# Revit family: 876-01-001-DN400-1200
name_source: partatom
category: Pipe Accessories
units: mm (PartAtom-declared; Revit-internal decimal feet)

## family parameters
Always vertical = Yes
Cut with Voids When Loaded = No
Part Type = Valve - Breaks Into
Round Connector Dimension = Use Diameter
Shared = No
Work Plane-Based = No

## types (18) — shared parameters
3 = 3 mm  [stored 0.00984252 ft]
876-0400-01-01102012 = DN400_PN10
876-0400-01-11102012 = DN400_PN16
876-0450-01-01102012 = DN450_PN10
876-0450-01-11102012 = DN450_PN16
876-0500-01-01102012 = DN500_PN10
876-0500-01-11102012 = DN500_PN16
876-0600-01-01102012 = DN600_PN10
876-0600-01-11102012 = DN600_PN16
876-0700-01-01102012 = DN700_PN10
876-0700-01-11102012 = DN700_PN16
876-0800-01-01102012 = DN800_PN10
876-0800-01-11102012 = DN800_PN16
876-0900-01-01102012 = DN900_PN10
876-0900-01-11102012 = DN900_PN16
876-1000-01-01102012 = DN1000_PN10
876-1000-01-11102012 = DN1000_PN16
876-1200-01-01102012 = DN1200_PN10
876-1200-01-11102012 = DN1200_PN16
Description_ = AVK NOZZLE CHECK VALVE, MULTI STEM
Search_table = 876-01-001-DN400-1200
URL product pages = https://www.avkvalves.com

## per-type parameters (varying)
| type | Bodywall_thickness | D | D1 | D2 | DN | Flange_thickness | Flange_thickness_2 | Flange_thickness_3 | Flange_thickness_4 | ID | ID_ref | ID_ref_2 | L | L1 | PCD |
| DN0400_PN10 | 210 mm  [stored 0.688976 ft] | 283 mm | 515 mm | 240 mm  [stored 0.787402 ft] | 400 mm | 20 mm  [stored 0.0656168 ft] | 10 mm  [stored 0.0328084 ft] | 30 mm  [stored 0.0984252 ft] | 40 mm  [stored 0.131234 ft] | 200 mm  [stored 0.656168 ft] | 180 mm  [stored 0.590551 ft] | 90 mm  [stored 0.295276 ft] | 310 mm | 1 mm  [stored 0.00328084 ft] | 127 mm |
| DN0400_PN16 | 210 mm  [stored 0.688976 ft] | 290 mm | 525 mm | 240 mm  [stored 0.787402 ft] | 400 mm | 20 mm  [stored 0.0656168 ft] | 10 mm  [stored 0.0328084 ft] | 30 mm  [stored 0.0984252 ft] | 40 mm  [stored 0.131234 ft] | 200 mm  [stored 0.656168 ft] | 180 mm  [stored 0.590551 ft] | 90 mm  [stored 0.295276 ft] | 310 mm | 1 mm  [stored 0.00328084 ft] | 127 mm |
| DN0450_PN16 | 235 mm  [stored 0.770997 ft] | 320 mm | 585 mm | 274 mm | 450 mm | 30 mm  [stored 0.0984252 ft] | 15 mm  [stored 0.0492126 ft] | 45 mm  [stored 0.147638 ft] | 60 mm  [stored 0.19685 ft] | 225 mm  [stored 0.738189 ft] | 195 mm  [stored 0.639764 ft] | 98 mm | 330 mm | 7 mm  [stored 0.0229659 ft] | 140 mm  [stored 0.459318 ft] |
| DN0500_PN10 | 260 mm | 335 mm | 620 mm | 291 mm | 500 mm | 30 mm  [stored 0.0984252 ft] | 15 mm  [stored 0.0492126 ft] | 45 mm  [stored 0.147638 ft] | 60 mm  [stored 0.19685 ft] | 250 mm | 220 mm  [stored 0.721785 ft] | 110 mm  [stored 0.360892 ft] | 350 mm | 5 mm  [stored 0.0164042 ft] | 157 mm |
| DN0450_PN10 | 235 mm  [stored 0.770997 ft] | 308 mm | 565 mm | 280 mm | 450 mm | 30 mm  [stored 0.0984252 ft] | 15 mm  [stored 0.0492126 ft] | 45 mm  [stored 0.147638 ft] | 60 mm  [stored 0.19685 ft] | 225 mm  [stored 0.738189 ft] | 195 mm  [stored 0.639764 ft] | 98 mm | 330 mm | 7 mm  [stored 0.0229659 ft] | 140 mm  [stored 0.459318 ft] |
| DN0500_PN16 | 260 mm | 358 mm | 650 mm | 305 mm | 500 mm | 30 mm  [stored 0.0984252 ft] | 15 mm  [stored 0.0492126 ft] | 45 mm  [stored 0.147638 ft] | 60 mm  [stored 0.19685 ft] | 250 mm | 220 mm  [stored 0.721785 ft] | 110 mm  [stored 0.360892 ft] | 350 mm | 5 mm  [stored 0.0164042 ft] | 157 mm |
| DN0600_PN10 | 310 mm | 390 mm | 725 mm | 341 mm | 600 mm | 30 mm  [stored 0.0984252 ft] | 15 mm  [stored 0.0492126 ft] | 45 mm  [stored 0.147638 ft] | 60 mm  [stored 0.19685 ft] | 300 mm | 270 mm | 135 mm  [stored 0.442913 ft] | 390 mm | 15 mm  [stored 0.0492126 ft] | 190 mm |
| DN0600_PN16 | 310 mm | 420 mm | 770 mm | 360 mm | 600 mm | 30 mm  [stored 0.0984252 ft] | 15 mm  [stored 0.0492126 ft] | 45 mm  [stored 0.147638 ft] | 60 mm  [stored 0.19685 ft] | 300 mm | 270 mm | 135 mm  [stored 0.442913 ft] | 390 mm | 15 mm  [stored 0.0492126 ft] | 190 mm |
| DN0700_PN10 | 360 mm | 448 mm | 840 mm | 397 mm | 700 mm | 40 mm  [stored 0.131234 ft] | 20 mm  [stored 0.0656168 ft] | 60 mm  [stored 0.19685 ft] | 80 mm  [stored 0.262467 ft] | 350 mm | 310 mm | 155 mm  [stored 0.50853 ft] | 430 mm | 3 mm  [stored 0.00984252 ft] | 220 mm  [stored 0.721785 ft] |
| DN0700_PN16 | 360 mm | 455 mm | 840 mm | 397 mm | 700 mm | 40 mm  [stored 0.131234 ft] | 20 mm  [stored 0.0656168 ft] | 60 mm  [stored 0.19685 ft] | 80 mm  [stored 0.262467 ft] | 350 mm | 310 mm | 155 mm  [stored 0.50853 ft] | 430 mm | 3 mm  [stored 0.00984252 ft] | 220 mm  [stored 0.721785 ft] |
| DN0800_PN10 | 410 mm | 508 mm | 950 mm | 451 mm | 800 mm | 40 mm  [stored 0.131234 ft] | 20 mm  [stored 0.0656168 ft] | 60 mm  [stored 0.19685 ft] | 80 mm  [stored 0.262467 ft] | 400 mm | 360 mm | 180 mm  [stored 0.590551 ft] | 470 mm | 12 mm  [stored 0.0393701 ft] | 253 mm |
| DN0800_PN16 | 410 mm | 513 mm | 950 mm | 451 mm | 800 mm | 40 mm  [stored 0.131234 ft] | 20 mm  [stored 0.0656168 ft] | 60 mm  [stored 0.19685 ft] | 80 mm  [stored 0.262467 ft] | 400 mm | 360 mm | 180 mm  [stored 0.590551 ft] | 470 mm | 12 mm  [stored 0.0393701 ft] | 253 mm |
| DN0900_PN10 | 460 mm | 558 mm | 1050 mm | 501 mm | 900 mm | 45 mm  [stored 0.147638 ft] | 23 mm | 68 mm | 90 mm  [stored 0.295276 ft] | 450 mm | 405 mm | 203 mm | 510 mm | 19 mm  [stored 0.062336 ft] | 285 mm |
| DN0900_PN16 | 460 mm | 563 mm | 1050 mm | 501 mm | 900 mm | 45 mm  [stored 0.147638 ft] | 23 mm | 68 mm | 90 mm  [stored 0.295276 ft] | 450 mm | 405 mm | 203 mm | 510 mm | 19 mm  [stored 0.062336 ft] | 285 mm |
| DN1000_PN10 | 510 mm | 615 mm | 1160 mm | 556 mm | 1000 mm | 50 mm  [stored 0.164042 ft] | 25 mm  [stored 0.082021 ft] | 75 mm | 100 mm  [stored 0.328084 ft] | 500 mm | 450 mm | 225 mm  [stored 0.738189 ft] | 550 mm | 28 mm  [stored 0.0918635 ft] | 317 mm |
| DN1000_PN16 | 510 mm | 628 mm | 1170 mm | 556 mm | 1000 mm | 50 mm  [stored 0.164042 ft] | 25 mm  [stored 0.082021 ft] | 75 mm | 100 mm  [stored 0.328084 ft] | 500 mm | 450 mm | 225 mm  [stored 0.738189 ft] | 550 mm | 28 mm  [stored 0.0918635 ft] | 317 mm |
| DN1200_PN10 | 610 mm | 728 mm | 1380 mm | 664 mm | 1200 mm | 60 mm  [stored 0.19685 ft] | 30 mm  [stored 0.0984252 ft] | 90 mm  [stored 0.295276 ft] | 120 mm  [stored 0.393701 ft] | 600 mm | 540 mm | 270 mm | 630 mm | 1 mm  [stored 0.00328084 ft] | 380 mm |
| DN1200_PN16 | 610 mm | 743 mm | 1390 mm | 664 mm | 1200 mm | 60 mm  [stored 0.19685 ft] | 30 mm  [stored 0.0984252 ft] | 90 mm  [stored 0.295276 ft] | 120 mm  [stored 0.393701 ft] | 600 mm | 540 mm | 270 mm | 630 mm | 1 mm  [stored 0.00328084 ft] | 380 mm |

note: [stored X ft] marks values corroborated as IEEE doubles in the binary element streams (Revit-internal decimal feet)

## geometry (parser evidence)
native form markers: Sweep x12
no freeform markers — native parametric forms only
